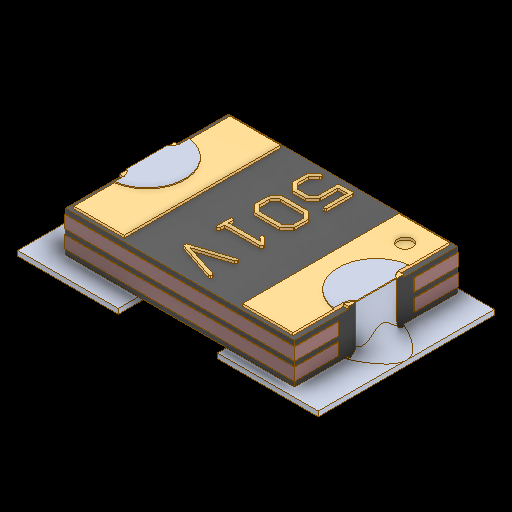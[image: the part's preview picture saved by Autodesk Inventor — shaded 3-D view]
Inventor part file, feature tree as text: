
AUTODESK INVENTOR PART (.ipt)
format: ipt  version: 2022 (Build 260153000, 153)  size: 411,648 bytes
history: native  units: in
note: dims shown in document units (in); Inventor stores cm internally (conversion verified against a paired STEP export)
features: mirror x1
ambient origin geometry x8: Origin, YZ Plane, XZ Plane, XY Plane, X Axis, Y Axis, Z Axis, Center Point
bodies: Solid1 (feature_tree)
feature tree (1):
  mirror  "Mirror5"
